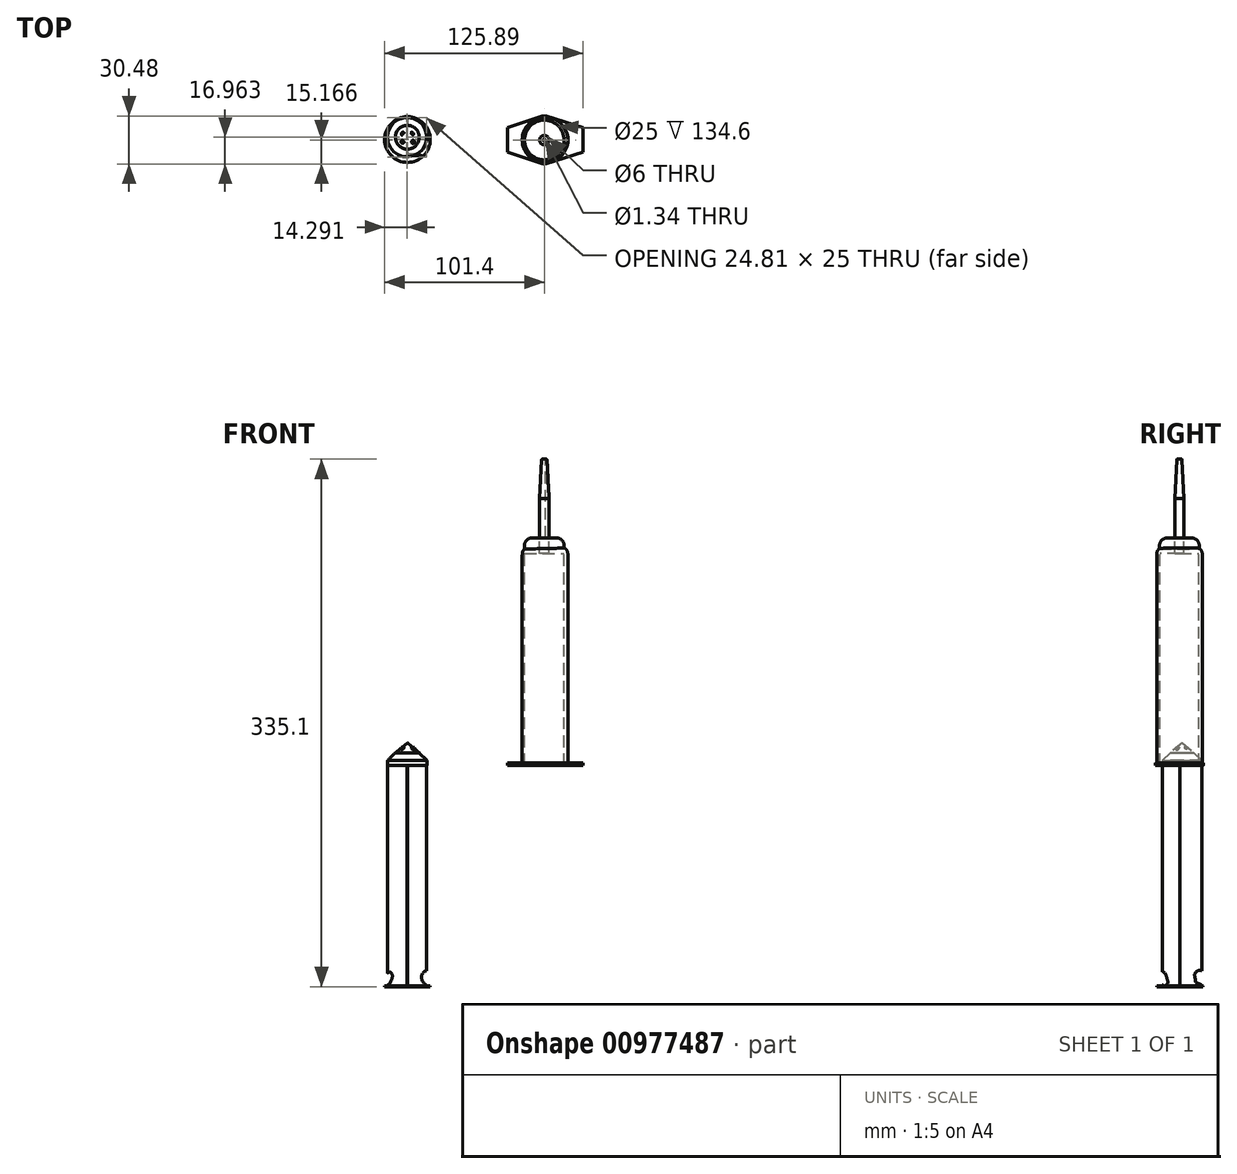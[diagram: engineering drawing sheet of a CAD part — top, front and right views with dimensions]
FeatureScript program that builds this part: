
annotation { "Feature Type Name" : "Feature", "Feature Type Description" : "" }
export const myFeature = defineFeature(function(context is Context, id is Id, definition is map)
    precondition{}
    {
        {
            var Q0;
            Q0=qCreatedBy(makeId("Top.planeOp"),FACE);
            var sketch = newSketch(context, id + "F0", { "sketchPlane" : qUnion([Q0])});
            skCircle(sketch, "E0", {"center": v(-58.67, 27.17) * mm, "radius": 12.5 * mm});
            skSolve(sketch);
        }
        {
            var Q0;
            Q0=makeQuery(id+"F0.imprint","IMPRINT",FACE,{"disambiguationData":[TD([[makeQuery(id+"F0.imprint","IMPRINT",EDGE,{"derivedFrom":sQuery(id+"F0.wireOp",EDGE,"E0")}),1.0]])]});
            extrude(context, id + "F1", {"entities" : qUnion([Q0]), "depth" : 8 * mm, "offsetDistance" : 25 * mm});
        }
        {
            var Q0;
            Q0=makeQuery(id+"F1.opExtrude","CAP_EDGE",EDGE,{"disambiguationData":[OSD([sQuery(id+"F0.wireOp",EDGE,"E0")])],"isStart":false});
            fillet(context, id + "F2", {"entities" : qUnion([Q0]), "radius" : 5 * mm, "tangentPropagation" : true, "rho" : 0, "crossSection" : FilletCrossSection.CONIC, "allowEdgeOverflow" : false});
        }
        {
            var Q0;
            Q0=makeQuery(id+"F1.opExtrude","CAP_FACE",FACE,{"disambiguationData":[OSD([sQuery(id+"F0.wireOp",EDGE,"E0")])],"isStart":true});
            var sketch = newSketch(context, id + "F3", { "sketchPlane" : qUnion([Q0])});
            skLineSegment(sketch, "E1.bottom", {"start": v(-58.67, -14.67) * mm, "end": v(-58.47, -14.67) * mm});
            skLineSegment(sketch, "E1.top", {"start": v(-58.67, -39.67) * mm, "end": v(-58.47, -39.67) * mm});
            skLineSegment(sketch, "E1.left", {"start": v(-58.67, -14.67) * mm, "end": v(-58.67, -39.67) * mm});
            skLineSegment(sketch, "E1.right", {"start": v(-58.47, -14.67) * mm, "end": v(-58.47, -39.67) * mm});
            skLineSegment(sketch, "E2.bottom", {"start": v(-46.27, -25.6) * mm, "end": v(-71.08, -25.6) * mm});
            skLineSegment(sketch, "E2.top", {"start": v(-46.27, -25.67) * mm, "end": v(-71.08, -25.67) * mm});
            skLineSegment(sketch, "E2.left", {"start": v(-46.27, -25.6) * mm, "end": v(-46.27, -25.67) * mm});
            skLineSegment(sketch, "E2.right", {"start": v(-71.08, -25.6) * mm, "end": v(-71.08, -25.67) * mm});
            skSolve(sketch);
        }
        {
            var Q0;
            {var subQ0=sQuery(id+"F3.wireOp",EDGE,"E1.top");Q0=makeQuery(id+"F3.imprint","IMPRINT",FACE,{"disambiguationData":[TD([[makeQuery(id+"F3.imprint","IMPRINT",EDGE,{"derivedFrom":subQ0}),1.0]])]});}
            var Q1;
            {var subQ0=sQuery(id+"F3.wireOp",EDGE,"E1.bottom");Q1=makeQuery(id+"F3.imprint","IMPRINT",FACE,{"disambiguationData":[TD([[makeQuery(id+"F3.imprint","IMPRINT",EDGE,{"derivedFrom":subQ0}),-1.0]])]});}
            var Q2;
            {var subQ5=sQuery(id+"F3.wireOp",EDGE,"E2.left");Q2=makeQuery(id+"F3.imprint","IMPRINT",FACE,{"disambiguationData":[TD([[makeQuery(id+"F3.imprint","IMPRINT",EDGE,{"derivedFrom":subQ5}),-1.0]])]});}
            var Q3;
            {var subQ0=sQuery(id+"F3.wireOp",EDGE,"E2.bottom");var subQ1=sQuery(id+"F3.wireOp",EDGE,"E1.right");var subQ2=makeQuery(id+"F3.imprint","INTERSECT",VERTEX,{"derivedFrom":[subQ1,subQ0]});Q3=makeQuery(id+"F3.imprint","IMPRINT",FACE,{"disambiguationData":[TD([[makeQuery(id+"F3.imprint","IMPRINT",EDGE,{"disambiguationData":[TD([[subQ2,-1.0]])],"derivedFrom":subQ1}),-1.0]])]});}
            var Q4;
            {var subQ0=sQuery(id+"F3.wireOp",EDGE,"E2.bottom");var subQ1=sQuery(id+"F3.wireOp",EDGE,"E1.left");var subQ2=makeQuery(id+"F3.imprint","INTERSECT",VERTEX,{"derivedFrom":[subQ1,subQ0]});Q4=makeQuery(id+"F3.imprint","IMPRINT",FACE,{"disambiguationData":[TD([[makeQuery(id+"F3.imprint","IMPRINT",EDGE,{"disambiguationData":[TD([[subQ2,-1.0]])],"derivedFrom":subQ1}),-1.0]])]});}
            var Q5;
            {var subQ3=sQuery(id+"F3.wireOp",EDGE,"E2.bottom");var subQ5=sQuery(id+"F3.wireOp",EDGE,"E1.right");var subQ6=makeQuery(id+"F3.imprint","INTERSECT",VERTEX,{"derivedFrom":[subQ5,subQ3]});Q5=makeQuery(id+"F3.imprint","IMPRINT",FACE,{"disambiguationData":[TD([[makeQuery(id+"F3.imprint","IMPRINT",EDGE,{"disambiguationData":[TD([[subQ6,1.0]])],"derivedFrom":subQ5}),-1.0]])]});}
            var Q6;
            {var subQ3=sQuery(id+"F3.wireOp",EDGE,"E2.top");var subQ5=sQuery(id+"F3.wireOp",EDGE,"E1.right");var subQ6=makeQuery(id+"F3.imprint","INTERSECT",VERTEX,{"derivedFrom":[subQ5,subQ3]});Q6=makeQuery(id+"F3.imprint","IMPRINT",FACE,{"disambiguationData":[TD([[makeQuery(id+"F3.imprint","IMPRINT",EDGE,{"disambiguationData":[TD([[subQ6,-1.0]])],"derivedFrom":subQ5}),-1.0]])]});}
            extrude(context, id + "F4", {"entities" : qUnion([Q0, Q1, Q2, Q3, Q4, Q5, Q6]), "operationType" : NewBodyOperationType.ADD, "depth" : 140 * mm, "offsetDistance" : 25 * mm});
        }
        {
            var Q0;
            Q0=makeQuery(id+"F4.opExtrude","CAP_FACE",FACE,{"disambiguationData":[OSD([sQuery(id+"F0.wireOp",EDGE,"E0"),sQuery(id+"F3.wireOp",EDGE,"E1.bottom"),sQuery(id+"F3.wireOp",EDGE,"E1.top"),sQuery(id+"F3.wireOp",EDGE,"E1.left"),sQuery(id+"F3.wireOp",EDGE,"E1.right"),sQuery(id+"F3.wireOp",EDGE,"E2.bottom"),sQuery(id+"F3.wireOp",EDGE,"E2.top"),sQuery(id+"F3.wireOp",EDGE,"E2.left")])],"isStart":false});
            var sketch = newSketch(context, id + "F5", { "sketchPlane" : qUnion([Q0])});
            skCircle(sketch, "E3", {"center": v(-58.47, -25.67) * mm, "radius": 14.5 * mm});
            skSolve(sketch);
        }
        {
            var Q0;
            Q0=makeQuery(id+"F5.imprint","IMPRINT",FACE,{"disambiguationData":[TD([[makeQuery(id+"F5.imprint","IMPRINT",EDGE,{"derivedFrom":sQuery(id+"F5.wireOp",EDGE,"E3")}),1.0]])]});
            extrude(context, id + "F6", {"entities" : qUnion([Q0]), "depth" : 0.6 * mm, "offsetDistance" : 25 * mm});
        }
        {
            var Q0;
            Q0=qCreatedBy(makeId("Top.planeOp"),FACE);
            var sketch = newSketch(context, id + "F7", { "sketchPlane" : qUnion([Q0])});
            skLineSegment(sketch, "E4.bottom", {"start": v(4.92, 40.95) * mm, "end": v(52.92, 40.95) * mm});
            skLineSegment(sketch, "E4.top", {"start": v(4.92, 9.95) * mm, "end": v(52.92, 9.95) * mm});
            skLineSegment(sketch, "E4.left", {"start": v(4.92, 40.95) * mm, "end": v(4.92, 9.95) * mm});
            skLineSegment(sketch, "E4.right", {"start": v(52.92, 40.95) * mm, "end": v(52.92, 9.95) * mm});
            skSolve(sketch);
        }
        {
            var Q0;
            Q0=makeQuery(id+"F7.imprint","IMPRINT",FACE,{"disambiguationData":[TD([[makeQuery(id+"F7.imprint","IMPRINT",EDGE,{"derivedFrom":sQuery(id+"F7.wireOp",EDGE,"E4.bottom")}),-1.0]])]});
            extrude(context, id + "F8", {"entities" : qUnion([Q0]), "depth" : 1.5 * mm, "offsetDistance" : 25 * mm});
        }
        {
            var Q0;
            Q0=makeQuery(id+"F8.opExtrude","CAP_FACE",FACE,{"disambiguationData":[OSD([sQuery(id+"F7.wireOp",EDGE,"E4.bottom"),sQuery(id+"F7.wireOp",EDGE,"E4.top"),sQuery(id+"F7.wireOp",EDGE,"E4.left"),sQuery(id+"F7.wireOp",EDGE,"E4.right")])],"isStart":false});
            var sketch = newSketch(context, id + "F9", { "sketchPlane" : qUnion([Q0])});
            skCircle(sketch, "E5", {"center": v(28.92, 25.45) * mm, "radius": 14.5 * mm});
            skSolve(sketch);
        }
        {
            var Q0;
            Q0=makeQuery(id+"F9.imprint","IMPRINT",FACE,{"disambiguationData":[TD([[makeQuery(id+"F9.imprint","IMPRINT",EDGE,{"derivedFrom":sQuery(id+"F9.wireOp",EDGE,"E5")}),1.0]])]});
            extrude(context, id + "F10", {"entities" : qUnion([Q0]), "operationType" : NewBodyOperationType.ADD, "depth" : 137 * mm, "offsetDistance" : 25 * mm});
        }
        {
            var Q0;
            Q0=makeQuery(id+"F10.opExtrude","CAP_EDGE",EDGE,{"disambiguationData":[OSD([sQuery(id+"F9.wireOp",EDGE,"E5")])],"isStart":false});
            fillet(context, id + "F11", {"entities" : qUnion([Q0]), "radius" : 5 * mm, "tangentPropagation" : true, "rho" : 0.5, "crossSection" : FilletCrossSection.CONIC, "allowEdgeOverflow" : false});
        }
        {
            var Q0;
            Q0=makeQuery(id+"F10.opExtrude","CAP_FACE",FACE,{"disambiguationData":[OSD([sQuery(id+"F9.wireOp",EDGE,"E5")])],"isStart":false});
            var sketch = newSketch(context, id + "F12", { "sketchPlane" : qUnion([Q0])});
            skCircle(sketch, "E6", {"center": v(28.43, 25.38) * mm, "radius": 4 * mm});
            skSolve(sketch);
        }
        {
            var Q0;
            Q0=makeQuery(id+"F12.imprint","IMPRINT",FACE,{"disambiguationData":[TD([[makeQuery(id+"F12.imprint","IMPRINT",EDGE,{"derivedFrom":sQuery(id+"F12.wireOp",EDGE,"E6")}),1.0]])]});
            extrude(context, id + "F13", {"entities" : qUnion([Q0]), "operationType" : NewBodyOperationType.ADD, "depth" : 31 * mm, "offsetDistance" : 25 * mm});
        }
        {
            var Q0;
            Q0=makeQuery(id+"F13.opExtrude","CAP_EDGE",EDGE,{"disambiguationData":[OSD([sQuery(id+"F12.wireOp",EDGE,"E6")])],"isStart":false});
            fillet(context, id + "F14", {"entities" : qUnion([Q0]), "radius" : 1 * mm, "tangentPropagation" : true, "allowEdgeOverflow" : false});
        }
        {
            var Q0;
            Q0=makeQuery(id+"F13.opExtrude","CAP_FACE",FACE,{"disambiguationData":[OSD([sQuery(id+"F12.wireOp",EDGE,"E6")])],"isStart":false});
            var sketch = newSketch(context, id + "F15", { "sketchPlane" : qUnion([Q0])});
            skCircle(sketch, "E7", {"center": v(28.43, 25.38) * mm, "radius": 3 * mm});
            skSolve(sketch);
        }
        {
            var Q0;
            Q0=sQuery(id+"F15.wireOp",VERTEX,"E7.center");
            var Q1;
            Q1=makeQuery(id+"F8.opExtrude","SWEPT_BODY",BODY,{"disambiguationData":[OSD([sQuery(id+"F7.wireOp",EDGE,"E4.bottom"),sQuery(id+"F7.wireOp",EDGE,"E4.top"),sQuery(id+"F7.wireOp",EDGE,"E4.left"),sQuery(id+"F7.wireOp",EDGE,"E4.right")])]});
            hole(context, id + "F16", {"style" : HoleStyle.C_BORE, "endStyle" : HoleEndStyle.THROUGH, "holeDiameter" : 25 * mm, "cBoreDiameter" : 25 * mm, "cBoreDepth" : 1 * mm, "majorDiameter" : 5 * mm, "isTappedThrough" : true, "tappedDepth" : 12.7 * mm, "tapClearance" : 3, "locations" : qUnion([Q0]), "scope" : qUnion([Q1])});
        }
        {
            var Q0;
            Q0 = qSketchRegion(id + "F15", true);
            extrude(context, id + "F17", {"entities" : qUnion([Q0]), "depth" : 25 * mm, "offsetDistance" : 25 * mm, "hasDraft" : true, "draftAngle" : 3 * degree, "draftPullDirection" : true, "hasSecondDirection" : true, "secondDirectionOppositeDirection" : true, "secondDirectionDepth" : 25 * mm});
        }
        {
            var Q0;
            Q0=makeQuery(id+"F17.opExtrude","CAP_FACE",FACE,{"disambiguationData":[OSD([sQuery(id+"F15.wireOp",EDGE,"E7")])],"isStart":true});
            var sketch = newSketch(context, id + "F18", { "sketchPlane" : qUnion([Q0])});
            skCircle(sketch, "E8", {"center": v(28.43, -25.38) * mm, "radius": 12.62 * mm});
            skSolve(sketch);
        }
        {
            var Q0;
            Q0=makeQuery(id+"F18.imprint","IMPRINT",FACE,{"disambiguationData":[TD([[makeQuery(id+"F18.imprint","IMPRINT",EDGE,{"derivedFrom":sQuery(id+"F18.wireOp",EDGE,"E8")}),1.0]])]});
            extrude(context, id + "F19", {"entities" : qUnion([Q0]), "operationType" : NewBodyOperationType.ADD, "depth" : 9.9 * mm, "offsetDistance" : 25 * mm});
        }
        {
            var Q0;
            Q0=makeQuery(id+"F19.opExtrude","CAP_EDGE",EDGE,{"disambiguationData":[OSD([sQuery(id+"F18.wireOp",EDGE,"E8")])],"isStart":true});
            fillet(context, id + "F20", {"entities" : qUnion([Q0]), "radius" : 5 * mm, "tangentPropagation" : true, "allowEdgeOverflow" : false});
        }
        {
            var Q0;
            Q0=makeQuery(id+"F1.opExtrude","CAP_FACE",FACE,{"disambiguationData":[OSD([sQuery(id+"F0.wireOp",EDGE,"E0")])],"isStart":false});
            var sketch = newSketch(context, id + "F21", { "sketchPlane" : qUnion([Q0])});
            skCircle(sketch, "E9", {"center": v(-58.54, 27.14) * mm, "radius": 7.57 * mm});
            skSolve(sketch);
        }
        {
            var Q0;
            Q0 = qSketchRegion(id + "F21", true);
            extrude(context, id + "F22", {"entities" : qUnion([Q0]), "operationType" : NewBodyOperationType.ADD, "depth" : 8.6 * mm, "offsetDistance" : 25 * mm, "hasDraft" : true, "draftAngle" : 50 * degree, "draftPullDirection" : true});
        }
        {
            var Q0;
            {var subQ0=sQuery(id+"F3.wireOp",EDGE,"E1.left");Q0=makeQuery(id+"F4.opExtrude","SWEPT_FACE",FACE,{"disambiguationData":[OSD([subQ0]),TDD([makeQuery(id+"F3.imprint","IMPRINT",EDGE,{"disambiguationData":[TD([[makeQuery(id+"F3.imprint","INTERSECT",VERTEX,{"derivedFrom":[subQ0,sQuery(id+"F3.wireOp",EDGE,"E2.bottom")]}),1.0]])],"derivedFrom":subQ0})])]});}
            var sketch = newSketch(context, id + "F23", { "sketchPlane" : qUnion([Q0])});
            skFitSpline(sketch, "E10", {"points": [v(-14.67, -131.1) * mm, v(-16.57, -132.8) * mm, v(-17.55, -135.37) * mm, v(-17.95, -138.4) * mm, v(-16.5, -140) * mm, v(-14.67, -139.19) * mm, v(-14.67, -131.1) * mm]});
            skSolve(sketch);
        }
        {
            var Q0;
            {var subQ0=sQuery(id+"F23.wireOp",EDGE,"E10");var subQ1=sQuery(id+"F3.wireOp",EDGE,"E1.left");var subQ2=makeQuery(id+"F4.opExtrude","CAP_EDGE",EDGE,{"disambiguationData":[OSD([subQ1]),TDD([makeQuery(id+"F3.imprint","IMPRINT",EDGE,{"disambiguationData":[TD([[makeQuery(id+"F3.imprint","INTERSECT",VERTEX,{"derivedFrom":[subQ1,sQuery(id+"F3.wireOp",EDGE,"E2.bottom")]}),1.0]])],"derivedFrom":subQ1})])],"isStart":false});var subQ3=makeQuery(id+"F23.imprint","INTERSECT",VERTEX,{"disambiguationData":[OD(0.0)],"derivedFrom":[subQ2,subQ0]});Q0=makeQuery(id+"F23.imprint","IMPRINT",FACE,{"disambiguationData":[TD([[makeQuery(id+"F23.imprint","IMPRINT",EDGE,{"disambiguationData":[TD([[subQ3,-1.0]])],"derivedFrom":subQ0}),1.0]])]});}
            var Q1;
            {var subQ0=sQuery(id+"F23.wireOp",EDGE,"E10");var subQ1=sQuery(id+"F3.wireOp",EDGE,"E1.left");var subQ4=makeQuery(id+"F4.opExtrude","CAP_EDGE",EDGE,{"disambiguationData":[OSD([subQ1]),TDD([makeQuery(id+"F3.imprint","IMPRINT",EDGE,{"disambiguationData":[TD([[makeQuery(id+"F3.imprint","INTERSECT",VERTEX,{"derivedFrom":[subQ1,sQuery(id+"F3.wireOp",EDGE,"E2.bottom")]}),1.0]])],"derivedFrom":subQ1})])],"isStart":false});var subQ5=makeQuery(id+"F23.imprint","INTERSECT",VERTEX,{"disambiguationData":[OD(0.0)],"derivedFrom":[subQ4,subQ0]});Q1=makeQuery(id+"F23.imprint","IMPRINT",FACE,{"disambiguationData":[TD([[makeQuery(id+"F23.imprint","IMPRINT",EDGE,{"disambiguationData":[TD([[subQ5,1.0]])],"derivedFrom":subQ0}),1.0]])]});}
            extrude(context, id + "F24", {"entities" : qUnion([Q0, Q1]), "operationType" : NewBodyOperationType.REMOVE, "oppositeDirection" : true, "depth" : 8.4 * mm, "offsetDistance" : 25 * mm});
        }
        {
            var Q0;
            {var subQ0=sQuery(id+"F3.wireOp",EDGE,"E1.left");Q0=makeQuery(id+"F4.opExtrude","SWEPT_FACE",FACE,{"disambiguationData":[OSD([subQ0]),TDD([makeQuery(id+"F3.imprint","IMPRINT",EDGE,{"disambiguationData":[TD([[makeQuery(id+"F3.imprint","INTERSECT",VERTEX,{"derivedFrom":[subQ0,sQuery(id+"F3.wireOp",EDGE,"E2.top")]}),-1.0]])],"derivedFrom":subQ0})])]});}
            var sketch = newSketch(context, id + "F25", { "sketchPlane" : qUnion([Q0])});
            skFitSpline(sketch, "E11", {"points": [v(-39.67, -130.71) * mm, v(-36, -131.17) * mm, v(-35, -133.15) * mm, v(-35.33, -134.8) * mm, v(-36, -137.82) * mm, v(-38.16, -138.87) * mm, v(-39.67, -139.13) * mm, v(-39.67, -130.71) * mm]});
            skSolve(sketch);
        }
        {
            var Q0;
            {var subQ0=sQuery(id+"F25.wireOp",EDGE,"E11");var subQ1=makeQuery(id+"F4.opExtrude","SWEPT_EDGE",EDGE,{"disambiguationData":[OSD([sQuery(id+"F0.wireOp",EDGE,"E0"),sQuery(id+"F3.wireOp",EDGE,"E1.top"),sQuery(id+"F3.wireOp",EDGE,"E1.left")])]});var subQ2=makeQuery(id+"F25.imprint","INTERSECT",VERTEX,{"disambiguationData":[OD(0.0)],"derivedFrom":[subQ1,subQ0]});Q0=makeQuery(id+"F25.imprint","IMPRINT",FACE,{"disambiguationData":[TD([[makeQuery(id+"F25.imprint","IMPRINT",EDGE,{"disambiguationData":[TD([[subQ2,1.0]])],"derivedFrom":subQ0}),-1.0]])]});}
            extrude(context, id + "F26", {"entities" : qUnion([Q0]), "operationType" : NewBodyOperationType.REMOVE, "oppositeDirection" : true, "depth" : 25 * mm, "offsetDistance" : 25 * mm});
        }
        {
            var Q0;
            {var subQ0=sQuery(id+"F3.wireOp",EDGE,"E2.top");Q0=makeQuery(id+"F4.opExtrude","SWEPT_FACE",FACE,{"disambiguationData":[OSD([subQ0]),TDD([makeQuery(id+"F3.imprint","IMPRINT",EDGE,{"disambiguationData":[TD([[makeQuery(id+"F3.imprint","INTERSECT",VERTEX,{"derivedFrom":[subQ0,sQuery(id+"F3.wireOp",EDGE,"E2.left")]}),-1.0]])],"derivedFrom":subQ0})])]});}
            var sketch = newSketch(context, id + "F27", { "sketchPlane" : qUnion([Q0])});
            skFitSpline(sketch, "E12", {"points": [v(46.27, -130.72) * mm, v(48.63, -132) * mm, v(49.66, -134.4) * mm, v(48.9, -136.85) * mm, v(46.27, -139.41) * mm, v(46.27, -130.72) * mm]});
            skSolve(sketch);
        }
        {
            var Q0;
            Q0 = qSketchRegion(id + "F27", true);
            extrude(context, id + "F28", {"entities" : qUnion([Q0]), "operationType" : NewBodyOperationType.REMOVE, "oppositeDirection" : true, "depth" : 25 * mm, "offsetDistance" : 25 * mm});
        }
        {
            var Q0;
            {var subQ0=sQuery(id+"F3.wireOp",EDGE,"E2.bottom");Q0=makeQuery(id+"F4.opExtrude","SWEPT_FACE",FACE,{"disambiguationData":[OSD([subQ0]),TDD([makeQuery(id+"F3.imprint","IMPRINT",EDGE,{"disambiguationData":[TD([[makeQuery(id+"F3.imprint","INTERSECT",VERTEX,{"derivedFrom":[sQuery(id+"F3.wireOp",EDGE,"E1.left"),subQ0]}),-1.0]])],"derivedFrom":subQ0})])]});}
            var sketch = newSketch(context, id + "F29", { "sketchPlane" : qUnion([Q0])});
            skFitSpline(sketch, "E13", {"points": [v(-71.07, -132.1) * mm, v(-69.12, -131.54) * mm, v(-68.07, -133.38) * mm, v(-68.24, -135.02) * mm, v(-69.2, -137.7) * mm, v(-71.07, -139.25) * mm, v(-71.07, -132.1) * mm]});
            skSolve(sketch);
        }
        {
            var Q0;
            Q0 = qSketchRegion(id + "F29", true);
            extrude(context, id + "F30", {"entities" : qUnion([Q0]), "operationType" : NewBodyOperationType.REMOVE, "oppositeDirection" : true, "depth" : 25 * mm, "offsetDistance" : 25 * mm});
        }
        {
            var Q0;
            Q0=makeQuery(id+"F17.opExtrude","CAP_FACE",FACE,{"disambiguationData":[OSD([sQuery(id+"F15.wireOp",EDGE,"E7")])],"isStart":false});
            var sketch = newSketch(context, id + "F31", { "sketchPlane" : qUnion([Q0])});
            skCircle(sketch, "E14", {"center": v(28.43, 25.38) * mm, "radius": 0.67 * mm});
            skSolve(sketch);
        }
        {
            var Q0;
            Q0=makeQuery(id+"F31.imprint","IMPRINT",FACE,{"disambiguationData":[TD([[makeQuery(id+"F31.imprint","IMPRINT",EDGE,{"derivedFrom":sQuery(id+"F31.wireOp",EDGE,"E14")}),1.0]])]});
            extrude(context, id + "F32", {"entities" : qUnion([Q0]), "operationType" : NewBodyOperationType.REMOVE, "oppositeDirection" : true, "depth" : 187.2 * mm, "offsetDistance" : 25 * mm});
        }
        {
            var Q0;
            Q0=makeQuery(id+"F8.opExtrude","CAP_FACE",FACE,{"disambiguationData":[OSD([sQuery(id+"F7.wireOp",EDGE,"E4.bottom"),sQuery(id+"F7.wireOp",EDGE,"E4.top"),sQuery(id+"F7.wireOp",EDGE,"E4.left"),sQuery(id+"F7.wireOp",EDGE,"E4.right")])],"isStart":true});
            var sketch = newSketch(context, id + "F33", { "sketchPlane" : qUnion([Q0])});
            skLineSegment(sketch, "E15", {"start": v(28.43, -25.38) * mm, "end": v(28.43, -40.95) * mm});
            skLineSegment(sketch, "E16", {"start": v(28.43, -40.95) * mm, "end": v(28.43, -25.38) * mm});
            skPoint(sketch, "E17.oppositeSnap0", {"position": v(28.43, -33.16) * mm});
            skLineSegment(sketch, "E17.bottom", {"start": v(4.92, -40.95) * mm, "end": v(52.92, -40.95) * mm});
            skLineSegment(sketch, "E17.top", {"start": v(4.92, -33.16) * mm, "end": v(52.92, -33.16) * mm});
            skLineSegment(sketch, "E17.left", {"start": v(4.92, -40.95) * mm, "end": v(4.92, -33.16) * mm});
            skLineSegment(sketch, "E17.right", {"start": v(52.92, -40.95) * mm, "end": v(52.92, -33.16) * mm});
            skLineSegment(sketch, "E18.bottom", {"start": v(4.92, -9.95) * mm, "end": v(52.92, -9.95) * mm});
            skLineSegment(sketch, "E18.top", {"start": v(4.92, -17.74) * mm, "end": v(52.92, -17.74) * mm});
            skLineSegment(sketch, "E18.left", {"start": v(4.92, -9.95) * mm, "end": v(4.92, -17.74) * mm});
            skLineSegment(sketch, "E18.right", {"start": v(52.92, -9.95) * mm, "end": v(52.92, -17.74) * mm});
            skLineSegment(sketch, "E19", {"start": v(4.92, -33.16) * mm, "end": v(4.92, -17.74) * mm});
            skLineSegment(sketch, "E20", {"start": v(52.92, -33.16) * mm, "end": v(52.92, -17.74) * mm});
            skLineSegment(sketch, "E21", {"start": v(52.92, -33.16) * mm, "end": v(28.43, -40.95) * mm});
            skLineSegment(sketch, "E22", {"start": v(28.43, -40.95) * mm, "end": v(4.92, -33.16) * mm});
            skLineSegment(sketch, "E23", {"start": v(4.92, -17.74) * mm, "end": v(28.43, -9.95) * mm});
            skLineSegment(sketch, "E24", {"start": v(28.43, -9.95) * mm, "end": v(52.92, -17.74) * mm});
            skSolve(sketch);
        }
        {
            var Q0;
            {var subQ0=sQuery(id+"F33.wireOp",EDGE,"E17.right");Q0=makeQuery(id+"F33.imprint","IMPRINT",FACE,{"disambiguationData":[TD([[makeQuery(id+"F33.imprint","IMPRINT",EDGE,{"derivedFrom":subQ0}),1.0]])]});}
            var Q1;
            {var subQ0=sQuery(id+"F33.wireOp",EDGE,"E17.left");Q1=makeQuery(id+"F33.imprint","IMPRINT",FACE,{"disambiguationData":[TD([[makeQuery(id+"F33.imprint","IMPRINT",EDGE,{"derivedFrom":subQ0}),-1.0]])]});}
            var Q2;
            {var subQ0=sQuery(id+"F33.wireOp",EDGE,"E18.left");Q2=makeQuery(id+"F33.imprint","IMPRINT",FACE,{"disambiguationData":[TD([[makeQuery(id+"F33.imprint","IMPRINT",EDGE,{"derivedFrom":subQ0}),-1.0]])]});}
            var Q3;
            {var subQ0=sQuery(id+"F33.wireOp",EDGE,"E18.right");Q3=makeQuery(id+"F33.imprint","IMPRINT",FACE,{"disambiguationData":[TD([[makeQuery(id+"F33.imprint","IMPRINT",EDGE,{"derivedFrom":subQ0}),1.0]])]});}
            extrude(context, id + "F34", {"entities" : qUnion([Q0, Q1, Q2, Q3]), "operationType" : NewBodyOperationType.REMOVE, "oppositeDirection" : true, "depth" : 25 * mm, "offsetDistance" : 25 * mm});
        }
        {
            var Q0;
            Q0=makeQuery(id+"F34.boolean.opBoolean","COPY",EDGE,{"derivedFrom":makeQuery(id+"F34.opExtrude","SWEPT_EDGE",EDGE,{"disambiguationData":[OSD([sQuery(id+"F33.wireOp",EDGE,"E17.top"),sQuery(id+"F33.wireOp",EDGE,"E17.left"),sQuery(id+"F33.wireOp",EDGE,"E19"),sQuery(id+"F33.wireOp",EDGE,"E22")])]})});
            var Q1;
            {var subQ0=sQuery(id+"F33.wireOp",EDGE,"E22");var subQ1=sQuery(id+"F33.wireOp",EDGE,"E21");var subQ2=sQuery(id+"F33.wireOp",EDGE,"E17.bottom");var subQ3=sQuery(id+"F33.wireOp",EDGE,"E16");Q1=makeQuery(id+"F34.boolean.opBoolean","MERGE",EDGE,{"derivedFrom":[],"fromTools":[makeQuery(id+"F34.opExtrude","SWEPT_EDGE",EDGE,{"disambiguationData":[OSD([subQ3,subQ2,subQ1,subQ0]),OD(0.0)]}),makeQuery(id+"F34.opExtrude","SWEPT_EDGE",EDGE,{"disambiguationData":[OSD([subQ3,subQ2,subQ1,subQ0]),OD(1.0)]})]});}
            var Q2;
            Q2=makeQuery(id+"F34.boolean.opBoolean","COPY",EDGE,{"derivedFrom":makeQuery(id+"F34.opExtrude","SWEPT_EDGE",EDGE,{"disambiguationData":[OSD([sQuery(id+"F33.wireOp",EDGE,"E17.top"),sQuery(id+"F33.wireOp",EDGE,"E17.right"),sQuery(id+"F33.wireOp",EDGE,"E20"),sQuery(id+"F33.wireOp",EDGE,"E21")])]})});
            var Q3;
            Q3=makeQuery(id+"F34.boolean.opBoolean","COPY",EDGE,{"derivedFrom":makeQuery(id+"F34.opExtrude","SWEPT_EDGE",EDGE,{"disambiguationData":[OSD([sQuery(id+"F33.wireOp",EDGE,"E18.top"),sQuery(id+"F33.wireOp",EDGE,"E18.right"),sQuery(id+"F33.wireOp",EDGE,"E20"),sQuery(id+"F33.wireOp",EDGE,"E24")])]})});
            var Q4;
            {var subQ0=sQuery(id+"F33.wireOp",EDGE,"E24");var subQ1=sQuery(id+"F33.wireOp",EDGE,"E23");var subQ2=sQuery(id+"F33.wireOp",EDGE,"E18.bottom");Q4=makeQuery(id+"F34.boolean.opBoolean","MERGE",EDGE,{"derivedFrom":[],"fromTools":[makeQuery(id+"F34.opExtrude","SWEPT_EDGE",EDGE,{"disambiguationData":[OSD([subQ2,subQ1,subQ0]),OD(0.0)]}),makeQuery(id+"F34.opExtrude","SWEPT_EDGE",EDGE,{"disambiguationData":[OSD([subQ2,subQ1,subQ0]),OD(1.0)]})]});}
            var Q5;
            Q5=makeQuery(id+"F34.boolean.opBoolean","COPY",EDGE,{"derivedFrom":makeQuery(id+"F34.opExtrude","SWEPT_EDGE",EDGE,{"disambiguationData":[OSD([sQuery(id+"F33.wireOp",EDGE,"E18.top"),sQuery(id+"F33.wireOp",EDGE,"E18.left"),sQuery(id+"F33.wireOp",EDGE,"E19"),sQuery(id+"F33.wireOp",EDGE,"E23")])]})});
            fillet(context, id + "F35", {"entities" : qUnion([Q0, Q1, Q2, Q3, Q4, Q5]), "radius" : 5 * mm, "tangentPropagation" : true, "allowEdgeOverflow" : false});
        }
        {
            var Q0;
            Q0=makeQuery(id+"F17.opExtrude","CAP_EDGE",EDGE,{"disambiguationData":[OSD([sQuery(id+"F15.wireOp",EDGE,"E7")])],"isStart":false});
            fillet(context, id + "F36", {"entities" : qUnion([Q0]), "radius" : .5 * mm, "tangentPropagation" : true, "allowEdgeOverflow" : false});
        }
        {
            var Q0;
            Q0=qCreatedBy(makeId("Top.planeOp"),FACE);
            var sketch = newSketch(context, id + "F37", { "sketchPlane" : qUnion([Q0])});
            skCircle(sketch, "E25", {"center": v(-61.38, 29.3) * mm, "radius": 1 * mm});
            skCircle(sketch, "E26", {"center": v(-55.7, 29.3) * mm, "radius": 1 * mm});
            skCircle(sketch, "E27", {"center": v(-61.57, 24.24) * mm, "radius": 1 * mm});
            skCircle(sketch, "E28", {"center": v(-54.98, 24.24) * mm, "radius": 1 * mm});
            skSolve(sketch);
        }
        {
            var Q0;
            Q0 = qSketchRegion(id + "F37", true);
            extrude(context, id + "F38", {"entities" : qUnion([Q0]), "operationType" : NewBodyOperationType.ADD, "depth" : 11.4 * mm, "offsetDistance" : 25 * mm});
        }
    });
